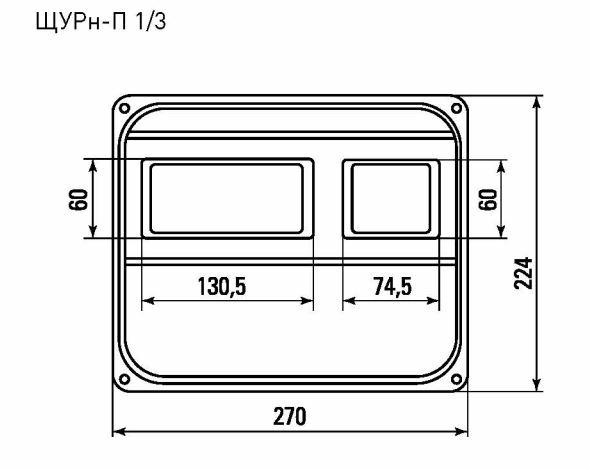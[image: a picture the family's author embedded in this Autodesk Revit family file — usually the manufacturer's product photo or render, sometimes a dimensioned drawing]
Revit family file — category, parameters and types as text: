
# Revit family: EKF_EE_ШкафСборкаAVTrivia_AVERES
name_source: partatom
category: Электрооборудование
units: mm (PartAtom-declared; Revit-internal decimal feet)

## family parameters
Всегда вертикально = Да
Конфигурация панели = Два столбца, слева направо
На основе рабочей плоскости = Нет
Общий = Нет
При загрузке вырезать с полостями = Нет
Размер круглого соединителя = Использовать диаметр
Тип детали = Щит
Точка расчета площади = Нет

## types (12) — shared parameters
IP = 30 мм
БП_IP30_400 = EKF_EE_БоковыеПанелиTrivia_AVERES : Боковые панели Г400 IP30 (2 шт) EKF AVERES
БП_IP30_600 = EKF_EE_БоковыеПанелиTrivia_AVERES : Боковые панели Г600 IP30 (2 шт) EKF AVERES
БП_IP30_800 = EKF_EE_БоковыеПанелиTrivia_AVERES : Боковые панели Г800 IP30 (2 шт) EKF AVERES
БП_IP55_400 = EKF_EE_БоковыеПанелиTrivia_AVERES : Боковые панели Г400 IP55 (2 шт) EKF AVERES
БП_IP55_600 = EKF_EE_БоковыеПанелиTrivia_AVERES : Боковые панели Г600 IP55 (2 шт)  EKF AVERES
БП_IP55_800 = EKF_EE_БоковыеПанелиTrivia_AVERES : Боковые панели Г800 IP55 (2 шт) EKF AVERES
ВП_IP30_300_400 = EKF_EE_ВерхняяПанельTrivia_AVERES : Верхняя панель Ш300 Г400 EKF AVERES
ВП_IP30_300_600 = EKF_EE_ВерхняяПанельTrivia_AVERES : Верхняя панель Ш300 Г600 EKF AVERES
ВП_IP30_300_800 = EKF_EE_ВерхняяПанельTrivia_AVERES : Верхняя панель Ш300 Г800 EKF AVERES
ВП_IP30_400_400 = EKF_EE_ВерхняяПанельTrivia_AVERES : Верхняя панель Ш400 Г400 EKF AVERES
ВП_IP30_400_600 = EKF_EE_ВерхняяПанельTrivia_AVERES : Верхняя панель Ш400 Г600 EKF AVERES
ВП_IP30_400_800 = EKF_EE_ВерхняяПанельTrivia_AVERES : Верхняя панель Ш400 Г800 EKF AVERES
ВП_IP30_600_400 = EKF_EE_ВерхняяПанельTrivia_AVERES : Верхняя панель Ш600 Г400 EKF AVERES
ВП_IP30_600_600 = EKF_EE_ВерхняяПанельTrivia_AVERES : Верхняя панель Ш600 Г600 EKF AVERES
ВП_IP30_600_800 = EKF_EE_ВерхняяПанельTrivia_AVERES : Верхняя панель Ш600 Г800 EKF AVERES
ВП_IP30_800_400 = EKF_EE_ВерхняяПанельTrivia_AVERES : Верхняя панель Ш800 Г400 EKF AVERES
ВП_IP30_800_600 = EKF_EE_ВерхняяПанельTrivia_AVERES : Верхняя панель Ш800 Г600 EKF AVERES
ВП_IP30_800_800 = EKF_EE_ВерхняяПанельTrivia_AVERES : Верхняя панель Ш800 Г800 EKF AVERES
ВП_IP55_300_400 = EKF_EE_ВерхняяПанельTrivia_AVERES : Верхняя панель Ш300 Г400 IP55 EKF AVERES
ВП_IP55_300_600 = EKF_EE_ВерхняяПанельTrivia_AVERES : Верхняя панель Ш300 Г600 IP55 EKF AVERES
ВП_IP55_300_800 = EKF_EE_ВерхняяПанельTrivia_AVERES : Верхняя панель Ш300 Г800 IP55 EKF AVERES
ВП_IP55_400_400 = EKF_EE_ВерхняяПанельTrivia_AVERES : Верхняя панель Ш400 Г400 IP55 EKF AVERES
ВП_IP55_400_600 = EKF_EE_ВерхняяПанельTrivia_AVERES : Верхняя панель Ш400 Г600 IP55 EKF AVERES
ВП_IP55_400_800 = EKF_EE_ВерхняяПанельTrivia_AVERES : Верхняя панель Ш400 Г800 IP55 EKF AVERES
ВП_IP55_600_400 = EKF_EE_ВерхняяПанельTrivia_AVERES : Верхняя панель Ш600 Г400 IP55 EKF AVERES
ВП_IP55_600_600 = EKF_EE_ВерхняяПанельTrivia_AVERES : Верхняя панель Ш600 Г600 IP55 EKF AVERES
ВП_IP55_600_800 = EKF_EE_ВерхняяПанельTrivia_AVERES : Верхняя панель Ш600 Г800 IP55 EKF AVERES
ВП_IP55_800_400 = EKF_EE_ВерхняяПанельTrivia_AVERES : Верхняя панель Ш800 Г400 IP55 EKF AVERES
ВП_IP55_800_600 = EKF_EE_ВерхняяПанельTrivia_AVERES : Верхняя панель Ш800 Г600 IP55 EKF AVERES
ВП_IP55_800_800 = EKF_EE_ВерхняяПанельTrivia_AVERES : Верхняя панель Ш800 Г800 IP55 EKF AVERES
Высота = 2013 мм
ДГ_IP30_300 = EKF_EE_ДверьГлухаяTrivia_AVERES : Дверь глухая металлическая Ш300 IP30 EKF AVERES
ДГ_IP30_400 = EKF_EE_ДверьГлухаяTrivia_AVERES : Дверь глухая металлическая Ш400 IP30 EKF AVERES
ДГ_IP30_600 = EKF_EE_ДверьГлухаяTrivia_AVERES : Дверь глухая металлическая Ш600 IP30 EKF AVERES
ДГ_IP30_800 = EKF_EE_ДверьГлухаяTrivia_AVERES : Дверь глухая металлическая Ш800 IP30 EKF AVERES
ДГ_IP55_300 = EKF_EE_ДверьГлухаяTrivia_AVERES : Дверь глухая металлическая Ш300 IP55 EKF AVERES
ДГ_IP55_400 = EKF_EE_ДверьГлухаяTrivia_AVERES : Дверь глухая металлическая Ш400 IP55 EKF AVERES
ДГ_IP55_600 = EKF_EE_ДверьГлухаяTrivia_AVERES : Дверь глухая металлическая Ш600 IP55 EKF AVERES
ДГ_IP55_800 = EKF_EE_ДверьГлухаяTrivia_AVERES : Дверь глухая металлическая Ш800 IP55 EKF AVERES
ДП_IP30_800 = EKF_EE_ДверьПрозрачнаяTrivia_AVERES : Дверь прозрачная Ш800 IP30 EKF AVERES
ДП_IP55_600 = EKF_EE_ДверьПрозрачнаяTrivia_AVERES : Дверь прозрачная Ш600 IP55 EKF AVERES
ДП_IP55_800 = EKF_EE_ДверьПрозрачнаяTrivia_AVERES : Дверь прозрачная Ш800 IP55 EKF AVERES
Дверь_Прозрачная = Нет
ЗП_IP30_300 = EKF_EE_ЗадняяПанельTrivia_AVERES : Задняя панель Ш300 IP30 EKF AVERES
ЗП_IP30_400 = EKF_EE_ЗадняяПанельTrivia_AVERES : Задняя панель Ш400 IP30 EKF AVERES
ЗП_IP30_600 = EKF_EE_ЗадняяПанельTrivia_AVERES : Задняя панель Ш600 IP30 EKF AVERES
ЗП_IP30_800 = EKF_EE_ЗадняяПанельTrivia_AVERES : Задняя панель Ш800 IP30 EKF AVERES
ЗП_IP55_300 = EKF_EE_ЗадняяПанельTrivia_AVERES : Задняя панель Ш300 IP55 EKF AVERES
ЗП_IP55_400 = EKF_EE_ЗадняяПанельTrivia_AVERES : Задняя панель Ш400 IP55 EKF AVERES
ЗП_IP55_600 = EKF_EE_ЗадняяПанельTrivia_AVERES : Задняя панель Ш600 IP55 EKF AVERES
ЗП_IP55_800 = EKF_EE_ЗадняяПанельTrivia_AVERES : Задняя панель Ш800 IP55 EKF AVERES
НСП_300_400 = EKF_EE_НижняяСальниковаяПанельГлухаяTrivia_AVERES : Нижняя сальниковая панель глухая Ш300 Г400 EKF AVERES
НСП_300_600 = EKF_EE_НижняяСальниковаяПанельГлухаяTrivia_AVERES : Нижняя сальниковая панель глухая Ш300 Г600 EKF AVERES
НСП_300_800 = EKF_EE_НижняяСальниковаяПанельГлухаяTrivia_AVERES : Нижняя сальниковая панель глухая Ш300 Г800 EKF AVERES
НСП_400_400 = EKF_EE_НижняяСальниковаяПанельГлухаяTrivia_AVERES : Нижняя сальниковая панель глухая Ш400 Г400 EKF AVERES
НСП_400_600 = EKF_EE_НижняяСальниковаяПанельГлухаяTrivia_AVERES : Нижняя сальниковая панель глухая Ш400 Г600 EKF AVERES
НСП_400_800 = EKF_EE_НижняяСальниковаяПанельГлухаяTrivia_AVERES : Нижняя сальниковая панель глухая Ш400 Г800 EKF AVERES
НСП_600_400 = EKF_EE_НижняяСальниковаяПанельГлухаяTrivia_AVERES : Нижняя сальниковая панель глухая Ш600 Г400 EKF AVERES
НСП_600_600 = EKF_EE_НижняяСальниковаяПанельГлухаяTrivia_AVERES : Нижняя сальниковая панель глухая Ш600 Г600 EKF AVERES
НСП_600_800 = EKF_EE_НижняяСальниковаяПанельГлухаяTrivia_AVERES : Нижняя сальниковая панель глухая Ш600 Г800 EKF AVERES
НСП_800_400 = EKF_EE_НижняяСальниковаяПанельГлухаяTrivia_AVERES : Нижняя сальниковая панель глухая Ш800 Г400 EKF AVERES
НСП_800_600 = EKF_EE_НижняяСальниковаяПанельГлухаяTrivia_AVERES : Нижняя сальниковая панель глухая Ш800 Г600 EKF AVERES
НСП_800_800 = EKF_EE_НижняяСальниковаяПанельГлухаяTrivia_AVERES : Нижняя сальниковая панель глухая Ш800 Г800 EKF AVERES
НСПС_300_400 = EKF_EE_НижняяСальниковаяПанельСоставнаяTrivia_AVERES : Нижняя сальниковая панель составная Ш300 Г400 EKF AVERES
НСПС_300_600 = EKF_EE_НижняяСальниковаяПанельСоставнаяTrivia_AVERES : Нижняя сальниковая панель составная Ш300 Г600 EKF AVERES
НСПС_300_800 = EKF_EE_НижняяСальниковаяПанельСоставнаяTrivia_AVERES : Нижняя сальниковая панель составная Ш300 Г800 EKF AVERES
НСПС_400_400 = EKF_EE_НижняяСальниковаяПанельСоставнаяTrivia_AVERES : Нижняя сальниковая панель составная Ш400 Г400 EKF AVERES
НСПС_400_600 = EKF_EE_НижняяСальниковаяПанельСоставнаяTrivia_AVERES : Нижняя сальниковая панель составная Ш400 Г600 EKF AVERES
НСПС_400_800 = EKF_EE_НижняяСальниковаяПанельСоставнаяTrivia_AVERES : Нижняя сальниковая панель составная Ш400 Г800 EKF AVERES
НСПС_600_400 = EKF_EE_НижняяСальниковаяПанельСоставнаяTrivia_AVERES : Нижняя сальниковая панель составная Ш600 Г400 EKF AVERES
НСПС_600_600 = EKF_EE_НижняяСальниковаяПанельСоставнаяTrivia_AVERES : Нижняя сальниковая панель составная Ш600 Г600 EKF AVERES
НСПС_600_800 = EKF_EE_НижняяСальниковаяПанельСоставнаяTrivia_AVERES : Нижняя сальниковая панель составная Ш600 Г800 EKF AVERES
НСПС_800_400 = EKF_EE_НижняяСальниковаяПанельСоставнаяTrivia_AVERES : Нижняя сальниковая панель составная Ш800 Г400 EKF AVERES
НСПС_800_600 = EKF_EE_НижняяСальниковаяПанельСоставнаяTrivia_AVERES : Нижняя сальниковая панель составная Ш800 Г600 EKF AVERES
НСПС_800_800 = EKF_EE_НижняяСальниковаяПанельСоставнаяTrivia_AVERES : Нижняя сальниковая панель составная Ш800 Г800 EKF AVERES
ПопПроф300 = EKF_EE_Поперечный профиль(4 шт)_EKF_AVERES : Поперечный профиль Ш300 (4 шт) EKF AVERES
ПопПроф400 = EKF_EE_Поперечный профиль(4 шт)_EKF_AVERES : Поперечный профиль Ш400 (4 шт) EKF AVERES
ПопПроф600 = EKF_EE_Поперечный профиль(4 шт)_EKF_AVERES : Поперечный профиль Ш600 (4 шт) EKF AVERES
ПопПроф800 = EKF_EE_Поперечный профиль(4 шт)_EKF_AVERES : Поперечный профиль Ш800 (4 шт) EKF AVERES
РШ400 = EKF_EE_РамаШкафаAVTrivia_AVERES : Рама шкафа AV Trivia В2000 Г400 (комплект из 2-х) EKF AVERES
РШ600 = EKF_EE_РамаШкафаAVTrivia_AVERES : Рама шкафа AV Trivia В2000 Г600 (комплект из 2-х) EKF AVERES
РШ800 = EKF_EE_РамаШкафаAVTrivia_AVERES : Рама шкафа AV Trivia В2000 Г800 (комплект из 2-х) EKF AVERES
Рым болт = Да
СальниковаяПанельСоставная = Нет
Сейсмоцоколь = Нет
Ц_300х400 = EKF_EE_ЦокольВСбореTrivia_AVERES : Цоколь в сборе Ш300 Г400
Ц_300х600 = EKF_EE_ЦокольВСбореTrivia_AVERES : Цоколь в сборе Ш300 Г600
Ц_300х800 = EKF_EE_ЦокольВСбореTrivia_AVERES : Цоколь в сборе Ш300 Г800
Ц_400х400 = EKF_EE_ЦокольВСбореTrivia_AVERES : Цоколь в сборе Ш400 Г400
Ц_400х600 = EKF_EE_ЦокольВСбореTrivia_AVERES : Цоколь в сборе Ш400 Г600
Ц_400х800 = EKF_EE_ЦокольВСбореTrivia_AVERES : Цоколь в сборе Ш400 Г800
Ц_600х400 = EKF_EE_ЦокольВСбореTrivia_AVERES : Цоколь в сборе Ш600 Г400
Ц_600х600 = EKF_EE_ЦокольВСбореTrivia_AVERES : Цоколь в сборе Ш600 Г600
Ц_600х800 = EKF_EE_ЦокольВСбореTrivia_AVERES : Цоколь в сборе Ш600 Г800
Ц_800х400 = EKF_EE_ЦокольВСбореTrivia_AVERES : Цоколь в сборе Ш800 Г400
Ц_800х600 = EKF_EE_ЦокольВСбореTrivia_AVERES : Цоколь в сборе Ш800 Г600
Ц_800х800 = EKF_EE_ЦокольВСбореTrivia_AVERES : Цоколь в сборе Ш800 Г800
ЦС_600х600 = EKF_EE_СейсмоцокольВСбореTrivia_AVERES : Сейсмоцоколь в сборе Ш600
ЦС_800х600 = EKF_EE_СейсмоцокольВСбореTrivia_AVERES : Сейсмоцоколь в сборе Ш800

## per-type parameters (varying)
| type | БоковыеПанели | БоковыеСтенки_Ширина | ВерхняяПанель | Глубина | Дверь | ДержательПластронов_Ширина | ЗадняяПанель | НижняяСальниковаяПанель | ПоперечныйПрофить | РамаШкафа | Цоколь | Ширина |
| Шкаф 300х400 | EKF_EE_БоковыеПанелиTrivia_AVERES : Боковые панели Г400 IP30 (2 шт) EKF AVERES | 338 мм | EKF_EE_ВерхняяПанельTrivia_AVERES : Верхняя панель Ш300 Г400 EKF AVERES | 410 мм | EKF_EE_ДверьГлухаяTrivia_AVERES : Дверь глухая металлическая Ш300 IP30 EKF AVERES | 225 мм | EKF_EE_ЗадняяПанельTrivia_AVERES : Задняя панель Ш300 IP30 EKF AVERES | EKF_EE_НижняяСальниковаяПанельГлухаяTrivia_AVERES : Нижняя сальниковая панель глухая Ш300 Г400 EKF AVERES | EKF_EE_Поперечный профиль(4 шт)_EKF_AVERES : Поперечный профиль Ш300 (4 шт) EKF AVERES | EKF_EE_РамаШкафаAVTrivia_AVERES : Рама шкафа AV Trivia В2000 Г400 (комплект из 2-х) EKF AVERES | EKF_EE_ЦокольВСбореTrivia_AVERES : Цоколь в сборе Ш300 Г400 | 310 мм |
| Шкаф 300х600 | EKF_EE_БоковыеПанелиTrivia_AVERES : Боковые панели Г600 IP30 (2 шт) EKF AVERES | 338 мм | EKF_EE_ВерхняяПанельTrivia_AVERES : Верхняя панель Ш300 Г600 EKF AVERES | 610 мм | EKF_EE_ДверьГлухаяTrivia_AVERES : Дверь глухая металлическая Ш300 IP30 EKF AVERES | 225 мм | EKF_EE_ЗадняяПанельTrivia_AVERES : Задняя панель Ш300 IP30 EKF AVERES | EKF_EE_НижняяСальниковаяПанельГлухаяTrivia_AVERES : Нижняя сальниковая панель глухая Ш300 Г600 EKF AVERES | EKF_EE_Поперечный профиль(4 шт)_EKF_AVERES : Поперечный профиль Ш300 (4 шт) EKF AVERES | EKF_EE_РамаШкафаAVTrivia_AVERES : Рама шкафа AV Trivia В2000 Г600 (комплект из 2-х) EKF AVERES | EKF_EE_ЦокольВСбореTrivia_AVERES : Цоколь в сборе Ш300 Г600 | 310 мм |
| Шкаф 300х800 | EKF_EE_БоковыеПанелиTrivia_AVERES : Боковые панели Г800 IP30 (2 шт) EKF AVERES | 338 мм | EKF_EE_ВерхняяПанельTrivia_AVERES : Верхняя панель Ш300 Г800 EKF AVERES | 810 мм | EKF_EE_ДверьГлухаяTrivia_AVERES : Дверь глухая металлическая Ш300 IP30 EKF AVERES | 225 мм | EKF_EE_ЗадняяПанельTrivia_AVERES : Задняя панель Ш300 IP30 EKF AVERES | EKF_EE_НижняяСальниковаяПанельГлухаяTrivia_AVERES : Нижняя сальниковая панель глухая Ш300 Г800 EKF AVERES | EKF_EE_Поперечный профиль(4 шт)_EKF_AVERES : Поперечный профиль Ш300 (4 шт) EKF AVERES | EKF_EE_РамаШкафаAVTrivia_AVERES : Рама шкафа AV Trivia В2000 Г800 (комплект из 2-х) EKF AVERES | EKF_EE_ЦокольВСбореTrivia_AVERES : Цоколь в сборе Ш300 Г800 | 310 мм |
| Шкаф 400х400 | EKF_EE_БоковыеПанелиTrivia_AVERES : Боковые панели Г400 IP30 (2 шт) EKF AVERES | 438 мм | EKF_EE_ВерхняяПанельTrivia_AVERES : Верхняя панель Ш400 Г400 EKF AVERES | 410 мм | EKF_EE_ДверьГлухаяTrivia_AVERES : Дверь глухая металлическая Ш400 IP30 EKF AVERES | 325 мм | EKF_EE_ЗадняяПанельTrivia_AVERES : Задняя панель Ш400 IP30 EKF AVERES | EKF_EE_НижняяСальниковаяПанельГлухаяTrivia_AVERES : Нижняя сальниковая панель глухая Ш400 Г400 EKF AVERES | EKF_EE_Поперечный профиль(4 шт)_EKF_AVERES : Поперечный профиль Ш400 (4 шт) EKF AVERES | EKF_EE_РамаШкафаAVTrivia_AVERES : Рама шкафа AV Trivia В2000 Г400 (комплект из 2-х) EKF AVERES | EKF_EE_ЦокольВСбореTrivia_AVERES : Цоколь в сборе Ш400 Г400 | 410 мм |
| Шкаф 400х600 | EKF_EE_БоковыеПанелиTrivia_AVERES : Боковые панели Г600 IP30 (2 шт) EKF AVERES | 438 мм | EKF_EE_ВерхняяПанельTrivia_AVERES : Верхняя панель Ш400 Г600 EKF AVERES | 610 мм | EKF_EE_ДверьГлухаяTrivia_AVERES : Дверь глухая металлическая Ш400 IP30 EKF AVERES | 325 мм | EKF_EE_ЗадняяПанельTrivia_AVERES : Задняя панель Ш400 IP30 EKF AVERES | EKF_EE_НижняяСальниковаяПанельГлухаяTrivia_AVERES : Нижняя сальниковая панель глухая Ш400 Г600 EKF AVERES | EKF_EE_Поперечный профиль(4 шт)_EKF_AVERES : Поперечный профиль Ш400 (4 шт) EKF AVERES | EKF_EE_РамаШкафаAVTrivia_AVERES : Рама шкафа AV Trivia В2000 Г600 (комплект из 2-х) EKF AVERES | EKF_EE_ЦокольВСбореTrivia_AVERES : Цоколь в сборе Ш400 Г600 | 410 мм |
| Шкаф 400х800 | EKF_EE_БоковыеПанелиTrivia_AVERES : Боковые панели Г800 IP30 (2 шт) EKF AVERES | 438 мм | EKF_EE_ВерхняяПанельTrivia_AVERES : Верхняя панель Ш400 Г800 EKF AVERES | 810 мм | EKF_EE_ДверьГлухаяTrivia_AVERES : Дверь глухая металлическая Ш400 IP30 EKF AVERES | 325 мм | EKF_EE_ЗадняяПанельTrivia_AVERES : Задняя панель Ш400 IP30 EKF AVERES | EKF_EE_НижняяСальниковаяПанельГлухаяTrivia_AVERES : Нижняя сальниковая панель глухая Ш400 Г800 EKF AVERES | EKF_EE_Поперечный профиль(4 шт)_EKF_AVERES : Поперечный профиль Ш400 (4 шт) EKF AVERES | EKF_EE_РамаШкафаAVTrivia_AVERES : Рама шкафа AV Trivia В2000 Г800 (комплект из 2-х) EKF AVERES | EKF_EE_ЦокольВСбореTrivia_AVERES : Цоколь в сборе Ш400 Г800 | 410 мм |
| Шкаф 600х400 | EKF_EE_БоковыеПанелиTrivia_AVERES : Боковые панели Г400 IP30 (2 шт) EKF AVERES | 638 мм | EKF_EE_ВерхняяПанельTrivia_AVERES : Верхняя панель Ш600 Г400 EKF AVERES | 410 мм | EKF_EE_ДверьГлухаяTrivia_AVERES : Дверь глухая металлическая Ш600 IP30 EKF AVERES | 525 мм | EKF_EE_ЗадняяПанельTrivia_AVERES : Задняя панель Ш600 IP30 EKF AVERES | EKF_EE_НижняяСальниковаяПанельГлухаяTrivia_AVERES : Нижняя сальниковая панель глухая Ш600 Г400 EKF AVERES | EKF_EE_Поперечный профиль(4 шт)_EKF_AVERES : Поперечный профиль Ш600 (4 шт) EKF AVERES | EKF_EE_РамаШкафаAVTrivia_AVERES : Рама шкафа AV Trivia В2000 Г400 (комплект из 2-х) EKF AVERES | EKF_EE_ЦокольВСбореTrivia_AVERES : Цоколь в сборе Ш600 Г400 | 610 мм |
| Шкаф 600х600 | EKF_EE_БоковыеПанелиTrivia_AVERES : Боковые панели Г600 IP30 (2 шт) EKF AVERES | 638 мм | EKF_EE_ВерхняяПанельTrivia_AVERES : Верхняя панель Ш600 Г600 EKF AVERES | 610 мм | EKF_EE_ДверьГлухаяTrivia_AVERES : Дверь глухая металлическая Ш600 IP30 EKF AVERES | 525 мм | EKF_EE_ЗадняяПанельTrivia_AVERES : Задняя панель Ш600 IP30 EKF AVERES | EKF_EE_НижняяСальниковаяПанельГлухаяTrivia_AVERES : Нижняя сальниковая панель глухая Ш600 Г600 EKF AVERES | EKF_EE_Поперечный профиль(4 шт)_EKF_AVERES : Поперечный профиль Ш600 (4 шт) EKF AVERES | EKF_EE_РамаШкафаAVTrivia_AVERES : Рама шкафа AV Trivia В2000 Г600 (комплект из 2-х) EKF AVERES | EKF_EE_ЦокольВСбореTrivia_AVERES : Цоколь в сборе Ш600 Г600 | 610 мм |
| Шкаф 600х800 | EKF_EE_БоковыеПанелиTrivia_AVERES : Боковые панели Г800 IP30 (2 шт) EKF AVERES | 638 мм | EKF_EE_ВерхняяПанельTrivia_AVERES : Верхняя панель Ш600 Г800 EKF AVERES | 810 мм | EKF_EE_ДверьГлухаяTrivia_AVERES : Дверь глухая металлическая Ш600 IP30 EKF AVERES | 525 мм | EKF_EE_ЗадняяПанельTrivia_AVERES : Задняя панель Ш600 IP30 EKF AVERES | EKF_EE_НижняяСальниковаяПанельГлухаяTrivia_AVERES : Нижняя сальниковая панель глухая Ш600 Г800 EKF AVERES | EKF_EE_Поперечный профиль(4 шт)_EKF_AVERES : Поперечный профиль Ш600 (4 шт) EKF AVERES | EKF_EE_РамаШкафаAVTrivia_AVERES : Рама шкафа AV Trivia В2000 Г800 (комплект из 2-х) EKF AVERES | EKF_EE_ЦокольВСбореTrivia_AVERES : Цоколь в сборе Ш600 Г800 | 610 мм |
| Шкаф 800х400 | EKF_EE_БоковыеПанелиTrivia_AVERES : Боковые панели Г400 IP30 (2 шт) EKF AVERES | 838 мм | EKF_EE_ВерхняяПанельTrivia_AVERES : Верхняя панель Ш800 Г400 EKF AVERES | 410 мм | EKF_EE_ДверьГлухаяTrivia_AVERES : Дверь глухая металлическая Ш800 IP30 EKF AVERES | 725 мм | EKF_EE_ЗадняяПанельTrivia_AVERES : Задняя панель Ш800 IP30 EKF AVERES | EKF_EE_НижняяСальниковаяПанельГлухаяTrivia_AVERES : Нижняя сальниковая панель глухая Ш800 Г400 EKF AVERES | EKF_EE_Поперечный профиль(4 шт)_EKF_AVERES : Поперечный профиль Ш800 (4 шт) EKF AVERES | EKF_EE_РамаШкафаAVTrivia_AVERES : Рама шкафа AV Trivia В2000 Г400 (комплект из 2-х) EKF AVERES | EKF_EE_ЦокольВСбореTrivia_AVERES : Цоколь в сборе Ш800 Г400 | 810 мм |
| Шкаф 800х600 | EKF_EE_БоковыеПанелиTrivia_AVERES : Боковые панели Г600 IP30 (2 шт) EKF AVERES | 838 мм | EKF_EE_ВерхняяПанельTrivia_AVERES : Верхняя панель Ш800 Г600 EKF AVERES | 610 мм | EKF_EE_ДверьГлухаяTrivia_AVERES : Дверь глухая металлическая Ш800 IP30 EKF AVERES | 725 мм | EKF_EE_ЗадняяПанельTrivia_AVERES : Задняя панель Ш800 IP30 EKF AVERES | EKF_EE_НижняяСальниковаяПанельГлухаяTrivia_AVERES : Нижняя сальниковая панель глухая Ш800 Г600 EKF AVERES | EKF_EE_Поперечный профиль(4 шт)_EKF_AVERES : Поперечный профиль Ш800 (4 шт) EKF AVERES | EKF_EE_РамаШкафаAVTrivia_AVERES : Рама шкафа AV Trivia В2000 Г600 (комплект из 2-х) EKF AVERES | EKF_EE_ЦокольВСбореTrivia_AVERES : Цоколь в сборе Ш800 Г600 | 810 мм |
| Шкаф 800х800 | EKF_EE_БоковыеПанелиTrivia_AVERES : Боковые панели Г800 IP30 (2 шт) EKF AVERES | 838 мм | EKF_EE_ВерхняяПанельTrivia_AVERES : Верхняя панель Ш800 Г800 EKF AVERES | 810 мм | EKF_EE_ДверьГлухаяTrivia_AVERES : Дверь глухая металлическая Ш800 IP30 EKF AVERES | 725 мм | EKF_EE_ЗадняяПанельTrivia_AVERES : Задняя панель Ш800 IP30 EKF AVERES | EKF_EE_НижняяСальниковаяПанельГлухаяTrivia_AVERES : Нижняя сальниковая панель глухая Ш800 Г800 EKF AVERES | EKF_EE_Поперечный профиль(4 шт)_EKF_AVERES : Поперечный профиль Ш800 (4 шт) EKF AVERES | EKF_EE_РамаШкафаAVTrivia_AVERES : Рама шкафа AV Trivia В2000 Г800 (комплект из 2-х) EKF AVERES | EKF_EE_ЦокольВСбореTrivia_AVERES : Цоколь в сборе Ш800 Г800 | 810 мм |
